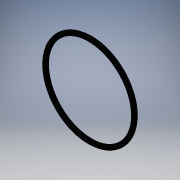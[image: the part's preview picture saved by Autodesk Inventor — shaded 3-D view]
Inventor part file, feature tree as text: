
AUTODESK INVENTOR PART (.ipt)
format: ipt  version: 2016 (Build 200138000, 138)  size: 126,976 bytes
history: native  units: in
note: dims shown in document units (in); Inventor stores cm internally (conversion verified against a paired STEP export)
features: revolve x1, sketch x1
ambient origin geometry x8: Origin, YZ Plane, XZ Plane, XY Plane, X Axis, Y Axis, Z Axis, Center Point
bodies: Solid1 (feature_tree)
feature tree (2):
  revolve  "Revolution1"  [1 undecoded]
  sketch  "Sketch1"  dims[d0=0.139in d1=2.484in d2=90.0deg]
note: 1 required parameter value undecoded (feature->parameter linkage not recoverable at this tier; creation-order binding heuristic only, values carry confidence <= 0.55)
